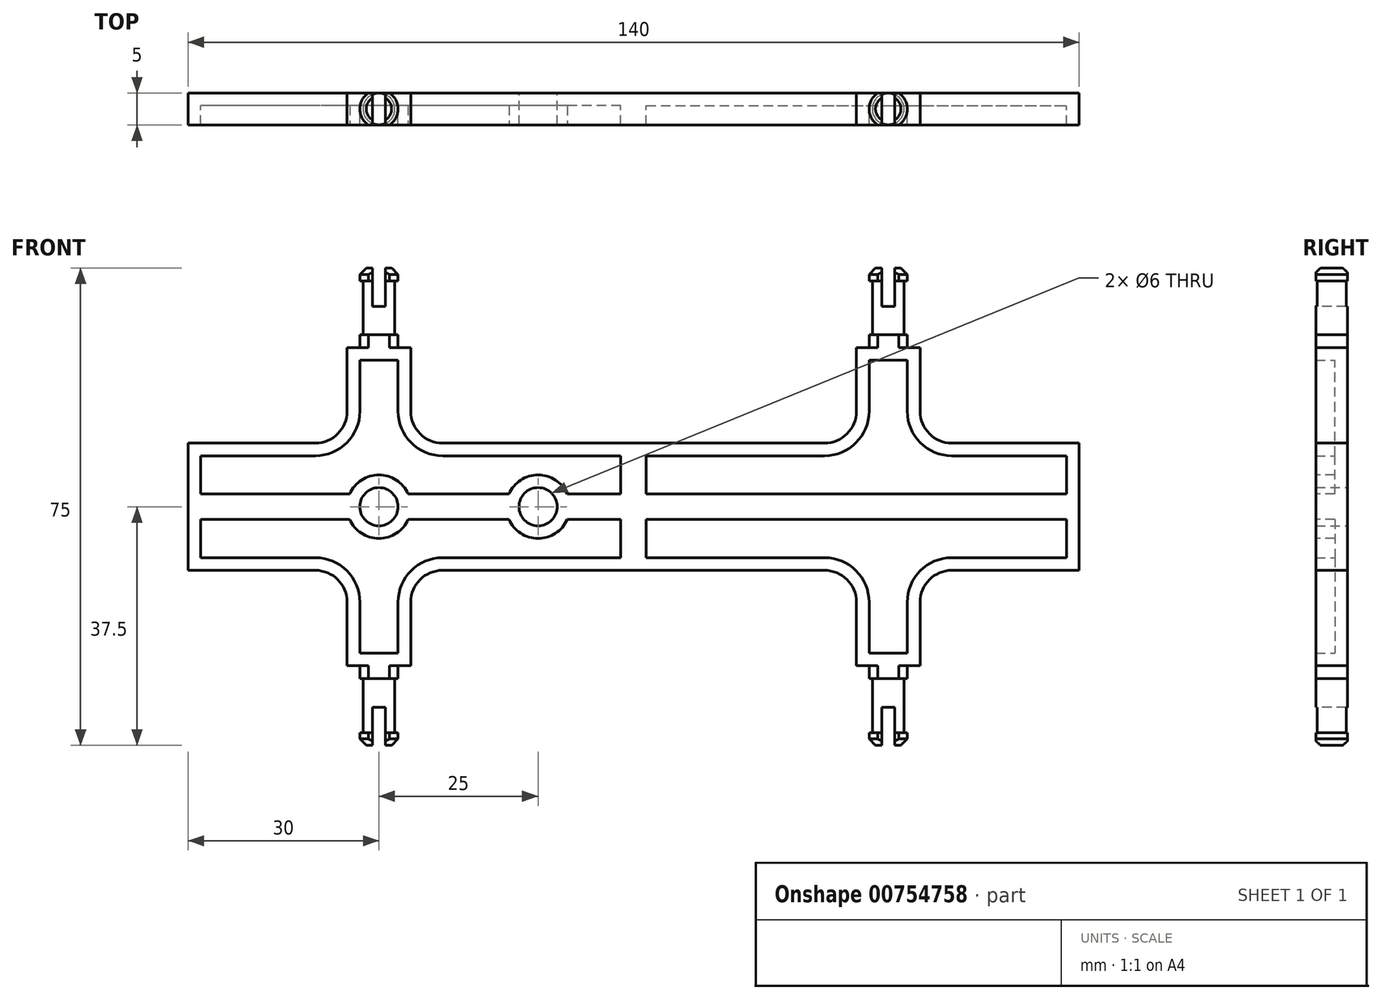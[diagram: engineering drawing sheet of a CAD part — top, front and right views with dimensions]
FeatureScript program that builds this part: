
annotation { "Feature Type Name" : "Feature", "Feature Type Description" : "" }
export const myFeature = defineFeature(function(context is Context, id is Id, definition is map)
    precondition{}
    {
        {
            var Q0;
            Q0=qCreatedBy(makeId("Front.planeOp"),FACE);
            var sketch = newSketch(context, id + "F0", { "sketchPlane" : qUnion([Q0])});
            skLineSegment(sketch, "E0.bottom", {"start": v(0, 0) * mm, "end": v(70, 0) * mm});
            skLineSegment(sketch, "E0.top", {"start": v(0, 10) * mm, "end": v(30, 10) * mm});
            skLineSegment(sketch, "E0.left", {"start": v(0, 0) * mm, "end": v(0, 10) * mm});
            skLineSegment(sketch, "E0.right", {"start": v(70, 0) * mm, "end": v(70, 10) * mm});
            skLineSegment(sketch, "E1.top", {"start": v(35, 25) * mm, "end": v(45, 25) * mm});
            skLineSegment(sketch, "E1.left", {"start": v(35, 15) * mm, "end": v(35, 25) * mm});
            skLineSegment(sketch, "E1.right", {"start": v(45, 15) * mm, "end": v(45, 25) * mm});
            skLineSegment(sketch, "E2.trimOffspring", {"start": v(50, 10) * mm, "end": v(70, 10) * mm});
            skPoint(sketch, "E3.visualSharp", {"position": v(35, 10) * mm});
            skArc(sketch, "E3.filletArc", {"start": v(30, 10) * mm, "mid": v(33.54, 11.46) * mm, "end": v(35, 15) * mm});
            skPoint(sketch, "E4.visualSharp", {"position": v(45, 10) * mm});
            skArc(sketch, "E4.filletArc", {"start": v(45, 15) * mm, "mid": v(46.46, 11.46) * mm, "end": v(50, 10) * mm});
            skSolve(sketch);
        }
        {
            var Q0;
            Q0=makeQuery(id+"F0.imprint","IMPRINT",FACE,{"disambiguationData":[TD([[makeQuery(id+"F0.imprint","IMPRINT",EDGE,{"derivedFrom":sQuery(id+"F0.wireOp",EDGE,"E0.bottom")}),1.0]])]});
            extrude(context, id + "F1", {"entities" : qUnion([Q0]), "depth" : 5 * mm, "offsetDistance" : 25 * mm, "symmetric" : true});
        }
        {
            var Q0;
            Q0=makeQuery(id+"F1.opExtrude","CAP_FACE",FACE,{"disambiguationData":[OSD([sQuery(id+"F0.wireOp",EDGE,"E0.bottom"),sQuery(id+"F0.wireOp",EDGE,"E0.top"),sQuery(id+"F0.wireOp",EDGE,"E0.left"),sQuery(id+"F0.wireOp",EDGE,"E0.right"),sQuery(id+"F0.wireOp",EDGE,"E1.top"),sQuery(id+"F0.wireOp",EDGE,"E1.left"),sQuery(id+"F0.wireOp",EDGE,"E1.right"),sQuery(id+"F0.wireOp",EDGE,"E2.trimOffspring"),sQuery(id+"F0.wireOp",EDGE,"E3.filletArc"),sQuery(id+"F0.wireOp",EDGE,"E4.filletArc")])],"isStart":false});
            shell(context, id + "F2", {"entities" : qUnion([Q0]), "thickness" : 2 * mm});
        }
        {
            var Q0;
            Q0=qCreatedBy(makeId("Front.planeOp"),FACE);
            var sketch = newSketch(context, id + "F3", { "sketchPlane" : qUnion([Q0])});
            skLineSegment(sketch, "E5", {"start": v(40, 25) * mm, "end": v(40, 37.5) * mm});
            skLineSegment(sketch, "E6", {"start": v(40, 37.5) * mm, "end": v(37, 37.5) * mm});
            skLineSegment(sketch, "E7", {"start": v(37, 37.5) * mm, "end": v(37, 35.5) * mm});
            skLineSegment(sketch, "E8", {"start": v(37, 35.5) * mm, "end": v(37.5, 35.5) * mm});
            skLineSegment(sketch, "E9", {"start": v(37.5, 35.5) * mm, "end": v(37.5, 27) * mm});
            skLineSegment(sketch, "E10", {"start": v(37.5, 27) * mm, "end": v(37, 27) * mm});
            skLineSegment(sketch, "E11", {"start": v(37, 27) * mm, "end": v(37, 25) * mm});
            skLineSegment(sketch, "E12", {"start": v(37, 25) * mm, "end": v(40, 25) * mm});
            skSolve(sketch);
        }
        {
            var Q0;
            Q0 = qSketchRegion(id + "F3", true);
            var Q1;
            Q1=sQuery(id+"F3.wireOp",EDGE,"E5");
            revolve(context, id + "F4", {"operationType" : NewBodyOperationType.ADD, "surfaceOperationType" : NewSurfaceOperationType.NEW, "entities" : qUnion([Q0]), "axis" : qUnion([Q1]), "revolveType" : RevolveType.FULL});
        }
        {
            var Q0;
            Q0=makeQuery(id+"F4.opRevolve","SWEPT_EDGE",EDGE,{"disambiguationData":[OSD([sQuery(id+"F3.wireOp",EDGE,"E6"),sQuery(id+"F3.wireOp",EDGE,"E7")])]});
            chamfer(context, id + "F5", {"entities" : qUnion([Q0]), "width" : 1 * mm, "tangentPropagation" : true});
        }
        {
            var Q0;
            Q0=makeQuery(id+"F4.opRevolve","SWEPT_FACE",FACE,{"disambiguationData":[OSD([sQuery(id+"F3.wireOp",EDGE,"E6")])]});
            var sketch = newSketch(context, id + "F6", { "sketchPlane" : qUnion([Q0])});
            skLineSegment(sketch, "E13.bottom", {"start": v(-2.87, 2.5) * mm, "end": v(72.13, 2.5) * mm});
            skLineSegment(sketch, "E13.top", {"start": v(-2.87, -2.5) * mm, "end": v(72.13, -2.5) * mm});
            skLineSegment(sketch, "E13.left", {"start": v(-2.87, 2.5) * mm, "end": v(-2.87, -2.5) * mm});
            skLineSegment(sketch, "E13.right", {"start": v(72.13, 2.5) * mm, "end": v(72.13, -2.5) * mm});
            skSolve(sketch);
        }
        {
            var Q0;
            Q0 = qSketchRegion(id + "F6", true);
            extrude(context, id + "F7", {"entities" : qUnion([Q0]), "operationType" : NewBodyOperationType.INTERSECT, "endBound" : BoundingType.THROUGH_ALL, "oppositeDirection" : true, "depth" : 25 * mm, "offsetDistance" : 25 * mm});
        }
        {
            var Q0;
            Q0=makeQuery(id+"F4.opRevolve","SWEPT_FACE",FACE,{"disambiguationData":[OSD([sQuery(id+"F3.wireOp",EDGE,"E6")])]});
            var sketch = newSketch(context, id + "F8", { "sketchPlane" : qUnion([Q0])});
            skLineSegment(sketch, "E14.bottom", {"start": v(39, 3.94) * mm, "end": v(41, 3.94) * mm});
            skLineSegment(sketch, "E14.top", {"start": v(39, -3.36) * mm, "end": v(41, -3.36) * mm});
            skLineSegment(sketch, "E14.left", {"start": v(39, 3.94) * mm, "end": v(39, -3.36) * mm});
            skLineSegment(sketch, "E14.right", {"start": v(41, 3.94) * mm, "end": v(41, -3.36) * mm});
            skSolve(sketch);
        }
        {
            var Q0;
            Q0 = qSketchRegion(id + "F8", true);
            extrude(context, id + "F9", {"entities" : qUnion([Q0]), "operationType" : NewBodyOperationType.REMOVE, "oppositeDirection" : true, "depth" : 6 * mm, "offsetDistance" : 25 * mm});
        }
        {
            var Q0;
            Q0=makeQuery(id+"F1.opExtrude","SWEPT_BODY",BODY,{"disambiguationData":[OSD([sQuery(id+"F0.wireOp",EDGE,"E0.bottom"),sQuery(id+"F0.wireOp",EDGE,"E0.top"),sQuery(id+"F0.wireOp",EDGE,"E0.left"),sQuery(id+"F0.wireOp",EDGE,"E0.right"),sQuery(id+"F0.wireOp",EDGE,"E1.top"),sQuery(id+"F0.wireOp",EDGE,"E1.left"),sQuery(id+"F0.wireOp",EDGE,"E1.right"),sQuery(id+"F0.wireOp",EDGE,"E2.trimOffspring"),sQuery(id+"F0.wireOp",EDGE,"E3.filletArc"),sQuery(id+"F0.wireOp",EDGE,"E4.filletArc")])]});
            var Q1;
            Q1=qCreatedBy(makeId("Top.planeOp"),FACE);
            mirror(context, id + "F10", {"operationType" : NewBodyOperationType.ADD, "entities" : qUnion([Q0]), "mirrorPlane" : qUnion([Q1])});
        }
        {
            var Q0;
            Q0=makeQuery(id+"F1.opExtrude","SWEPT_BODY",BODY,{"disambiguationData":[OSD([sQuery(id+"F0.wireOp",EDGE,"E0.bottom"),sQuery(id+"F0.wireOp",EDGE,"E0.top"),sQuery(id+"F0.wireOp",EDGE,"E0.left"),sQuery(id+"F0.wireOp",EDGE,"E0.right"),sQuery(id+"F0.wireOp",EDGE,"E1.top"),sQuery(id+"F0.wireOp",EDGE,"E1.left"),sQuery(id+"F0.wireOp",EDGE,"E1.right"),sQuery(id+"F0.wireOp",EDGE,"E2.trimOffspring"),sQuery(id+"F0.wireOp",EDGE,"E3.filletArc"),sQuery(id+"F0.wireOp",EDGE,"E4.filletArc")])]});
            var Q1;
            Q1=qCreatedBy(makeId("Right.planeOp"),FACE);
            mirror(context, id + "F11", {"operationType" : NewBodyOperationType.ADD, "entities" : qUnion([Q0]), "mirrorPlane" : qUnion([Q1])});
        }
        {
            var Q0;
            {var subQ0=makeQuery(id+"F7.boolean.opBoolean","MERGE",FACE,{"derivedFrom":[makeQuery(id+"F1.opExtrude","CAP_FACE",FACE,{"disambiguationData":[OSD([sQuery(id+"F0.wireOp",EDGE,"E0.bottom"),sQuery(id+"F0.wireOp",EDGE,"E0.top"),sQuery(id+"F0.wireOp",EDGE,"E0.left"),sQuery(id+"F0.wireOp",EDGE,"E0.right"),sQuery(id+"F0.wireOp",EDGE,"E1.top"),sQuery(id+"F0.wireOp",EDGE,"E1.left"),sQuery(id+"F0.wireOp",EDGE,"E1.right"),sQuery(id+"F0.wireOp",EDGE,"E2.trimOffspring"),sQuery(id+"F0.wireOp",EDGE,"E3.filletArc"),sQuery(id+"F0.wireOp",EDGE,"E4.filletArc")])],"isStart":false}),makeQuery(id+"F7.boolean.toolComplement.opBoolean","COPY",FACE,{"derivedFrom":makeQuery(id+"F7.opExtrude","SWEPT_FACE",FACE,{"disambiguationData":[OSD([sQuery(id+"F6.wireOp",EDGE,"E13.top")])]})})]});var subQ1=makeQuery(id+"F10.boolean.opBoolean","MERGE",FACE,{"derivedFrom":[subQ0,makeQuery(id+"F10.opPattern","COPY",FACE,{"derivedFrom":subQ0,"instanceName":"1"})]});Q0=makeQuery(id+"F11.boolean.opBoolean","MERGE",FACE,{"derivedFrom":[subQ1,makeQuery(id+"F11.opPattern","COPY",FACE,{"derivedFrom":subQ1,"instanceName":"1"})]});}
            var sketch = newSketch(context, id + "F12", { "sketchPlane" : qUnion([Q0])});
            skCircle(sketch, "E15", {"center": v(-40, 0) * mm, "radius": 5 * mm});
            skCircle(sketch, "E16", {"center": v(-15, 0) * mm, "radius": 5 * mm});
            skSolve(sketch);
        }
        {
            var Q0;
            Q0 = qSketchRegion(id + "F12", true);
            extrude(context, id + "F13", {"entities" : qUnion([Q0]), "operationType" : NewBodyOperationType.ADD, "endBound" : BoundingType.UP_TO_NEXT, "oppositeDirection" : true, "depth" : 25 * mm, "offsetDistance" : 25 * mm});
        }
        {
            var Q0;
            {var subQ0=makeQuery(id+"F7.boolean.opBoolean","MERGE",FACE,{"derivedFrom":[makeQuery(id+"F1.opExtrude","CAP_FACE",FACE,{"disambiguationData":[OSD([sQuery(id+"F0.wireOp",EDGE,"E0.bottom"),sQuery(id+"F0.wireOp",EDGE,"E0.top"),sQuery(id+"F0.wireOp",EDGE,"E0.left"),sQuery(id+"F0.wireOp",EDGE,"E0.right"),sQuery(id+"F0.wireOp",EDGE,"E1.top"),sQuery(id+"F0.wireOp",EDGE,"E1.left"),sQuery(id+"F0.wireOp",EDGE,"E1.right"),sQuery(id+"F0.wireOp",EDGE,"E2.trimOffspring"),sQuery(id+"F0.wireOp",EDGE,"E3.filletArc"),sQuery(id+"F0.wireOp",EDGE,"E4.filletArc")])],"isStart":false}),makeQuery(id+"F7.boolean.toolComplement.opBoolean","COPY",FACE,{"derivedFrom":makeQuery(id+"F7.opExtrude","SWEPT_FACE",FACE,{"disambiguationData":[OSD([sQuery(id+"F6.wireOp",EDGE,"E13.top")])]})})]});var subQ1=makeQuery(id+"F10.boolean.opBoolean","MERGE",FACE,{"derivedFrom":[subQ0,makeQuery(id+"F10.opPattern","COPY",FACE,{"derivedFrom":subQ0,"instanceName":"1"})]});Q0=makeQuery(id+"F13.boolean.opBoolean","MERGE",FACE,{"derivedFrom":[makeQuery(id+"F11.boolean.opBoolean","MERGE",FACE,{"derivedFrom":[subQ1,makeQuery(id+"F11.opPattern","COPY",FACE,{"derivedFrom":subQ1,"instanceName":"1"})]}),makeQuery(id+"F13.opExtrude","CAP_FACE",FACE,{"disambiguationData":[OSD([sQuery(id+"F12.wireOp",EDGE,"E15")])],"isStart":true}),makeQuery(id+"F13.opExtrude","CAP_FACE",FACE,{"disambiguationData":[OSD([sQuery(id+"F12.wireOp",EDGE,"E16")])],"isStart":true})]});}
            var sketch = newSketch(context, id + "F14", { "sketchPlane" : qUnion([Q0])});
            skPoint(sketch, "E17", {"position": v(-40, 0) * mm});
            skPoint(sketch, "E18", {"position": v(-15, 0) * mm});
            skSolve(sketch);
        }
        {
            var Q0;
            Q0=sQuery(id+"F14.wireOp",VERTEX,"E17");
            var Q1;
            Q1=sQuery(id+"F14.wireOp",VERTEX,"E18");
            var Q2;
            Q2=makeQuery(id+"F1.opExtrude","SWEPT_BODY",BODY,{"disambiguationData":[OSD([sQuery(id+"F0.wireOp",EDGE,"E0.bottom"),sQuery(id+"F0.wireOp",EDGE,"E0.top"),sQuery(id+"F0.wireOp",EDGE,"E0.left"),sQuery(id+"F0.wireOp",EDGE,"E0.right"),sQuery(id+"F0.wireOp",EDGE,"E1.top"),sQuery(id+"F0.wireOp",EDGE,"E1.left"),sQuery(id+"F0.wireOp",EDGE,"E1.right"),sQuery(id+"F0.wireOp",EDGE,"E2.trimOffspring"),sQuery(id+"F0.wireOp",EDGE,"E3.filletArc"),sQuery(id+"F0.wireOp",EDGE,"E4.filletArc")])]});
            hole(context, id + "F15", {"style" : HoleStyle.SIMPLE, "endStyle" : HoleEndStyle.THROUGH, "holeDiameter" : 6 * mm, "majorDiameter" : 5 * mm, "isTappedThrough" : true, "tappedDepth" : 12 * mm, "tapClearance" : 3, "locations" : qUnion([Q0, Q1]), "scope" : qUnion([Q2])});
        }
    });
